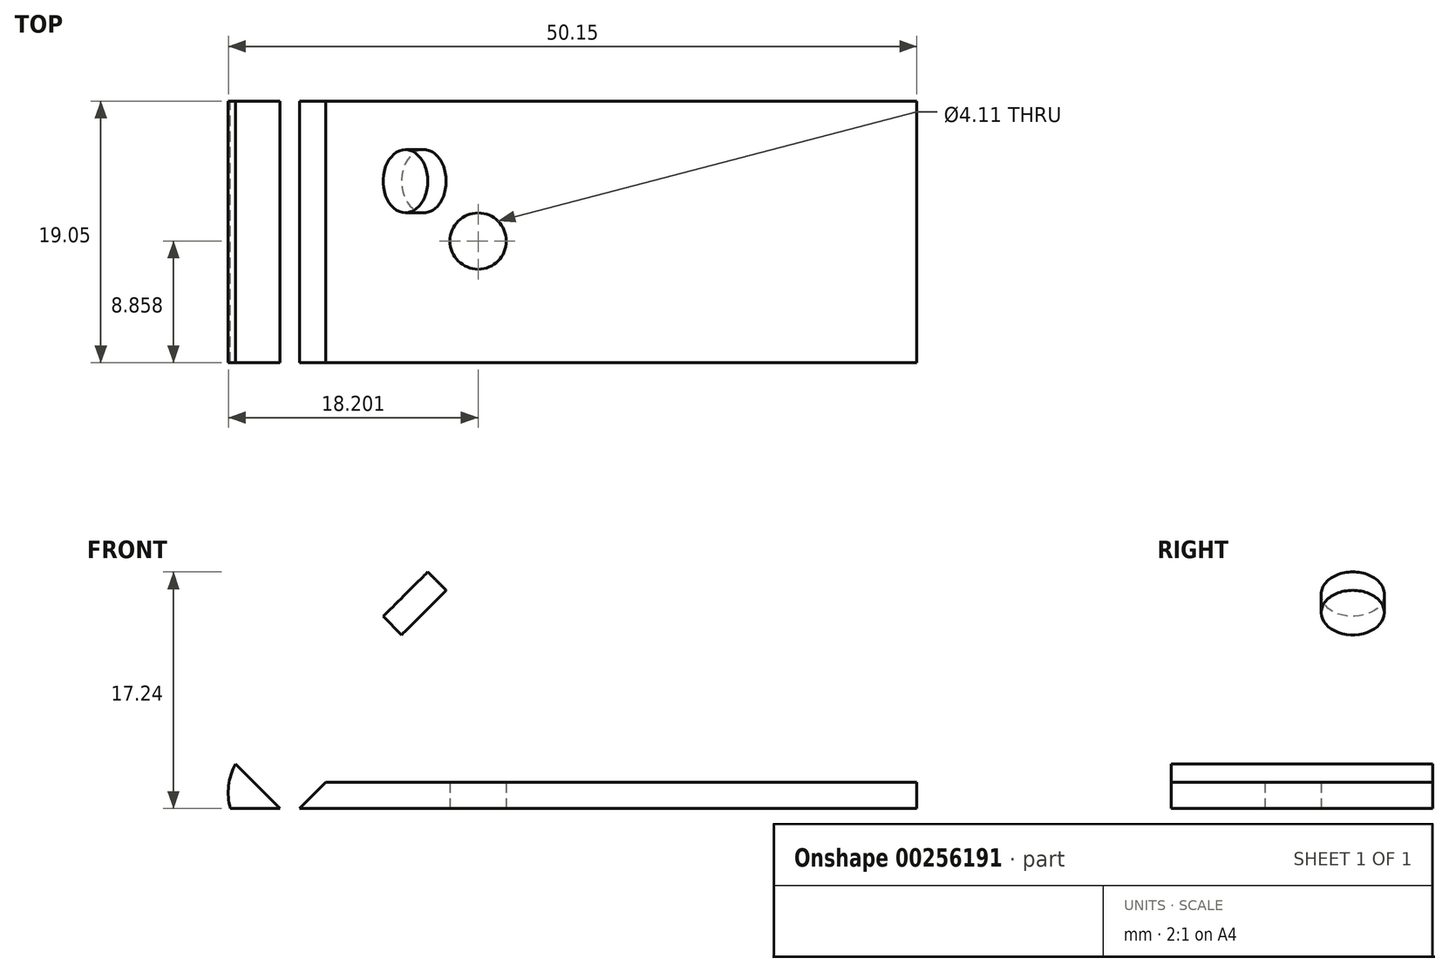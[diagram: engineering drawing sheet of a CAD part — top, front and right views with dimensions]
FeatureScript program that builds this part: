
annotation { "Feature Type Name" : "Feature", "Feature Type Description" : "" }
export const myFeature = defineFeature(function(context is Context, id is Id, definition is map)
    precondition{}
    {
        {
            var Q0;
            Q0=qCreatedBy(makeId("Front.planeOp"),FACE);
            var sketch = newSketch(context, id + "F0", { "sketchPlane" : qUnion([Q0])});
            skLineSegment(sketch, "E0", {"start": v(11.75, 1.9) * mm, "end": v(29.43, 19.58) * mm});
            skLineSegment(sketch, "E1", {"start": v(29.43, 19.58) * mm, "end": v(28.09, 20.92) * mm});
            skLineSegment(sketch, "E2", {"start": v(28.09, 20.92) * mm, "end": v(10.4, 3.24) * mm});
            skPoint(sketch, "E3.end.orphan", {"position": v(10.03, 0) * mm});
            skPoint(sketch, "E4.end.orphan", {"position": v(29.43, 0.54) * mm});
            skLineSegment(sketch, "E5", {"start": v(10.03, 0) * mm, "end": v(60.03, 0) * mm});
            skLineSegment(sketch, "E6", {"start": v(60.03, 0) * mm, "end": v(60.03, 1.9) * mm});
            skLineSegment(sketch, "E7", {"start": v(60.03, 1.9) * mm, "end": v(11.75, 1.9) * mm});
            skArc(sketch, "E8", {"start": v(10.4, 3.24) * mm, "mid": v(9.9, 1.66) * mm, "end": v(10.03, 0) * mm});
            skSolve(sketch);
        }
        {
            var Q0;
            Q0=makeQuery(id+"F0.imprint","IMPRINT",FACE,{"disambiguationData":[TD([[makeQuery(id+"F0.imprint","IMPRINT",EDGE,{"derivedFrom":sQuery(id+"F0.wireOp",EDGE,"E0")}),1.0]])]});
            extrude(context, id + "F1", {"entities" : qUnion([Q0]), "depth" : 19.05 * mm});
        }
        {
            var Q0;
            Q0=qCreatedBy(makeId("Top.planeOp"),FACE);
            var sketch = newSketch(context, id + "F2", { "sketchPlane" : qUnion([Q0])});
            skLineSegment(sketch, "E9", {"start": v(60.08, -10.2) * mm, "end": v(28.08, -10.2) * mm});
            skCircle(sketch, "E10", {"center": v(28.08, -10.2) * mm, "radius": 2.05 * mm});
            skSolve(sketch);
        }
        {
            var Q0;
            Q0=makeQuery(id+"F1.opExtrude","SWEPT_FACE",FACE,{"disambiguationData":[OSD([sQuery(id+"F0.wireOp",EDGE,"E2")])]});
            var sketch = newSketch(context, id + "F3", { "sketchPlane" : qUnion([Q0])});
            skLineSegment(sketch, "E11", {"start": v(19.05, 34.65) * mm, "end": v(19.05, 27.15) * mm});
            skLineSegment(sketch, "E12", {"start": v(19.05, 27.15) * mm, "end": v(14.55, 27.15) * mm});
            skCircle(sketch, "E13", {"center": v(14.55, 27.15) * mm, "radius": 2.3 * mm});
            skCircle(sketch, "E14.MirrorC", {"center": v(5.83, 27.15) * mm, "radius": 2.3 * mm});
            skSolve(sketch);
        }
        {
            var Q0;
            Q0=makeQuery(id+"F3.imprint","IMPRINT",FACE,{"disambiguationData":[TD([[makeQuery(id+"F3.imprint","IMPRINT",EDGE,{"derivedFrom":sQuery(id+"F3.wireOp",EDGE,"E13")}),1.0]])]});
            var Q1;
            Q1=makeQuery(id+"F3.imprint","IMPRINT",FACE,{"disambiguationData":[TD([[makeQuery(id+"F3.imprint","IMPRINT",EDGE,{"derivedFrom":sQuery(id+"F3.wireOp",EDGE,"E14.MirrorC")}),-1.0]])]});
            extrude(context, id + "F4", {"entities" : qUnion([Q0, Q1]), "operationType" : NewBodyOperationType.REMOVE, "oppositeDirection" : true, "depth" : 5.6 * mm});
        }
        {
            var Q0;
            Q0=makeQuery(id+"F2.imprint","IMPRINT",FACE,{"disambiguationData":[TD([[makeQuery(id+"F2.imprint","IMPRINT",EDGE,{"derivedFrom":sQuery(id+"F2.wireOp",EDGE,"E10")}),1.0]])]});
            extrude(context, id + "F5", {"entities" : qUnion([Q0]), "operationType" : NewBodyOperationType.REMOVE, "depth" : 5.84 * mm});
        }
    });
